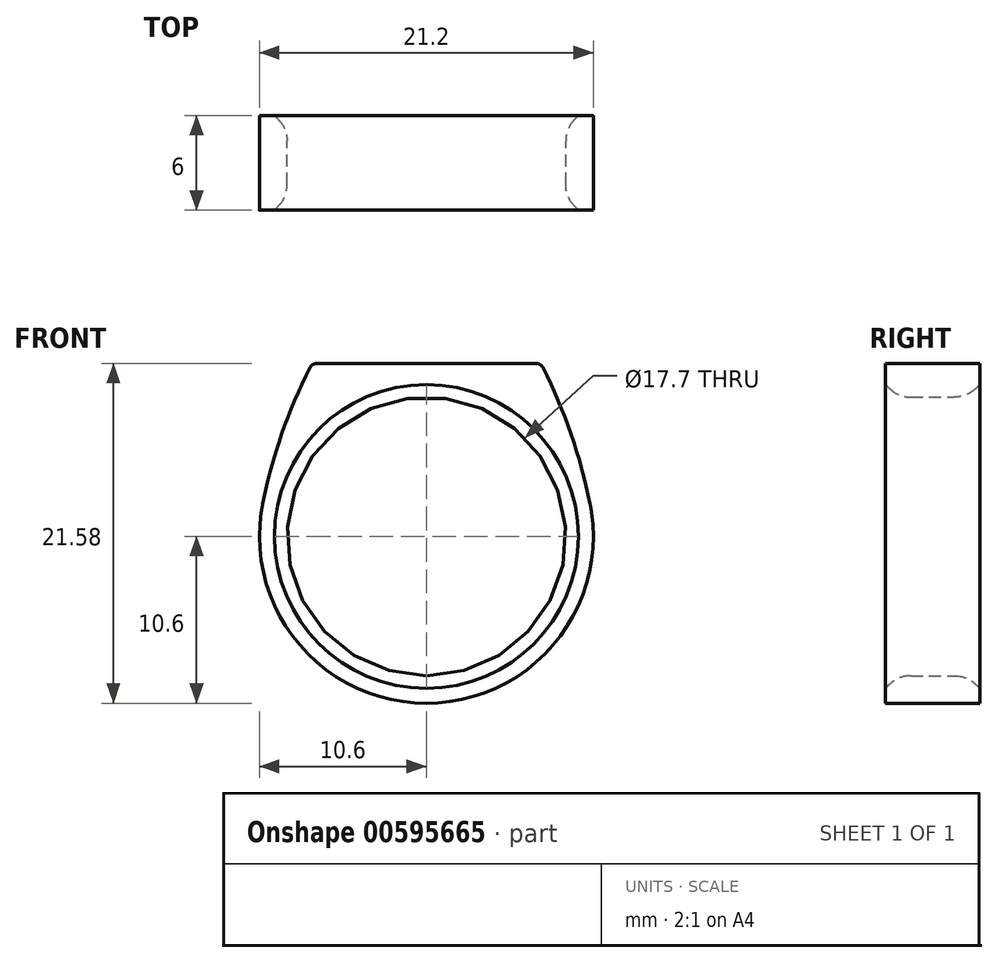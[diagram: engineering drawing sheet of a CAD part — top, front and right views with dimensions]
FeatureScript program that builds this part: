
annotation { "Feature Type Name" : "Feature", "Feature Type Description" : "" }
export const myFeature = defineFeature(function(context is Context, id is Id, definition is map)
    precondition{}
    {
        {
            var Q0;
            Q0=qCreatedBy(makeId("Front.planeOp"),FACE);
            var sketch = newSketch(context, id + "F0", { "sketchPlane" : qUnion([Q0])});
            skCircle(sketch, "E0", {"center": v(0, 0) * mm, "radius": 8.85 * mm});
            skCircle(sketch, "E1.0", {"center": v(0, 0) * mm, "radius": 10.6 * mm});
            skLineSegment(sketch, "E2", {"start": v(-7.27, 10.98) * mm, "end": v(0, 10.98) * mm});
            skLineSegment(sketch, "E3.MirrorCS", {"start": v(7.27, 10.98) * mm, "end": v(0, 10.98) * mm});
            skArc(sketch, "E4", {"start": v(-7.27, 10.98) * mm, "mid": v(-9.16, 6.58) * mm, "end": v(-10.42, 1.95) * mm});
            skArc(sketch, "E5.MirrorCS", {"start": v(7.27, 10.98) * mm, "mid": v(9.16, 6.58) * mm, "end": v(10.42, 1.95) * mm});
            skSolve(sketch);
        }
        {
            var Q0;
            Q0=makeQuery(id+"F0.imprint","IMPRINT",FACE,{"disambiguationData":[TD([[makeQuery(id+"F0.imprint","IMPRINT",EDGE,{"derivedFrom":sQuery(id+"F0.wireOp",EDGE,"E0")}),-1.0]])]});
            var Q1;
            {var subQ1=sQuery(id+"F0.wireOp",EDGE,"E2");Q1=makeQuery(id+"F0.imprint","IMPRINT",FACE,{"disambiguationData":[TD([[makeQuery(id+"F0.imprint","IMPRINT",EDGE,{"derivedFrom":subQ1}),-1.0]])]});}
            extrude(context, id + "F1", {"entities" : qUnion([Q0, Q1]), "depth" : 3 * mm, "offsetDistance" : 25 * mm, "hasSecondDirection" : true, "secondDirectionOppositeDirection" : true, "secondDirectionDepth" : 3 * mm});
        }
        {
            var Q0;
            Q0=makeQuery(id+"F1.opExtrude","SWEPT_EDGE",EDGE,{"disambiguationData":[OSD([sQuery(id+"F0.wireOp",EDGE,"E1.0"),sQuery(id+"F0.wireOp",EDGE,"E4")])]});
            var Q1;
            Q1=makeQuery(id+"F1.opExtrude","SWEPT_EDGE",EDGE,{"disambiguationData":[OSD([sQuery(id+"F0.wireOp",EDGE,"E1.0"),sQuery(id+"F0.wireOp",EDGE,"E5.MirrorCS")])]});
            fillet(context, id + "F2", {"entities" : qUnion([Q0, Q1]), "radius" : 10 * mm, "tangentPropagation" : true, "allowEdgeOverflow" : false});
        }
        {
            var Q0;
            Q0=makeQuery(id+"F1.opExtrude","CAP_EDGE",EDGE,{"disambiguationData":[OSD([sQuery(id+"F0.wireOp",EDGE,"E0")])],"isStart":true});
            var Q1;
            Q1=makeQuery(id+"F1.opExtrude","CAP_EDGE",EDGE,{"disambiguationData":[OSD([sQuery(id+"F0.wireOp",EDGE,"E0")])],"isStart":false});
            chamfer(context, id + "F3", {"entities" : qUnion([Q0, Q1]), "width" : .8 * mm, "tangentPropagation" : true});
        }
        {
            var Q0;
            Q0=makeQuery(id+"F1.opExtrude","SWEPT_EDGE",EDGE,{"disambiguationData":[OSD([sQuery(id+"F0.wireOp",EDGE,"E2"),sQuery(id+"F0.wireOp",EDGE,"E4")])]});
            var Q1;
            Q1=makeQuery(id+"F1.opExtrude","SWEPT_EDGE",EDGE,{"disambiguationData":[OSD([sQuery(id+"F0.wireOp",EDGE,"E3.MirrorCS"),sQuery(id+"F0.wireOp",EDGE,"E5.MirrorCS")])]});
            fillet(context, id + "F4", {"entities" : qUnion([Q0, Q1]), "radius" : 0.47 * mm, "tangentPropagation" : true, "allowEdgeOverflow" : false});
        }
        {
            var Q0;
            Q0=makeQuery(id+"F1.opExtrude","SWEPT_FACE",FACE,{"disambiguationData":[OSD([sQuery(id+"F0.wireOp",EDGE,"E0")])]});
            fillet(context, id + "F5", {"entities" : qUnion([Q0]), "radius" : 2 * mm, "rho" : 0.5, "crossSection" : FilletCrossSection.CONIC, "allowEdgeOverflow" : false});
        }
    });
